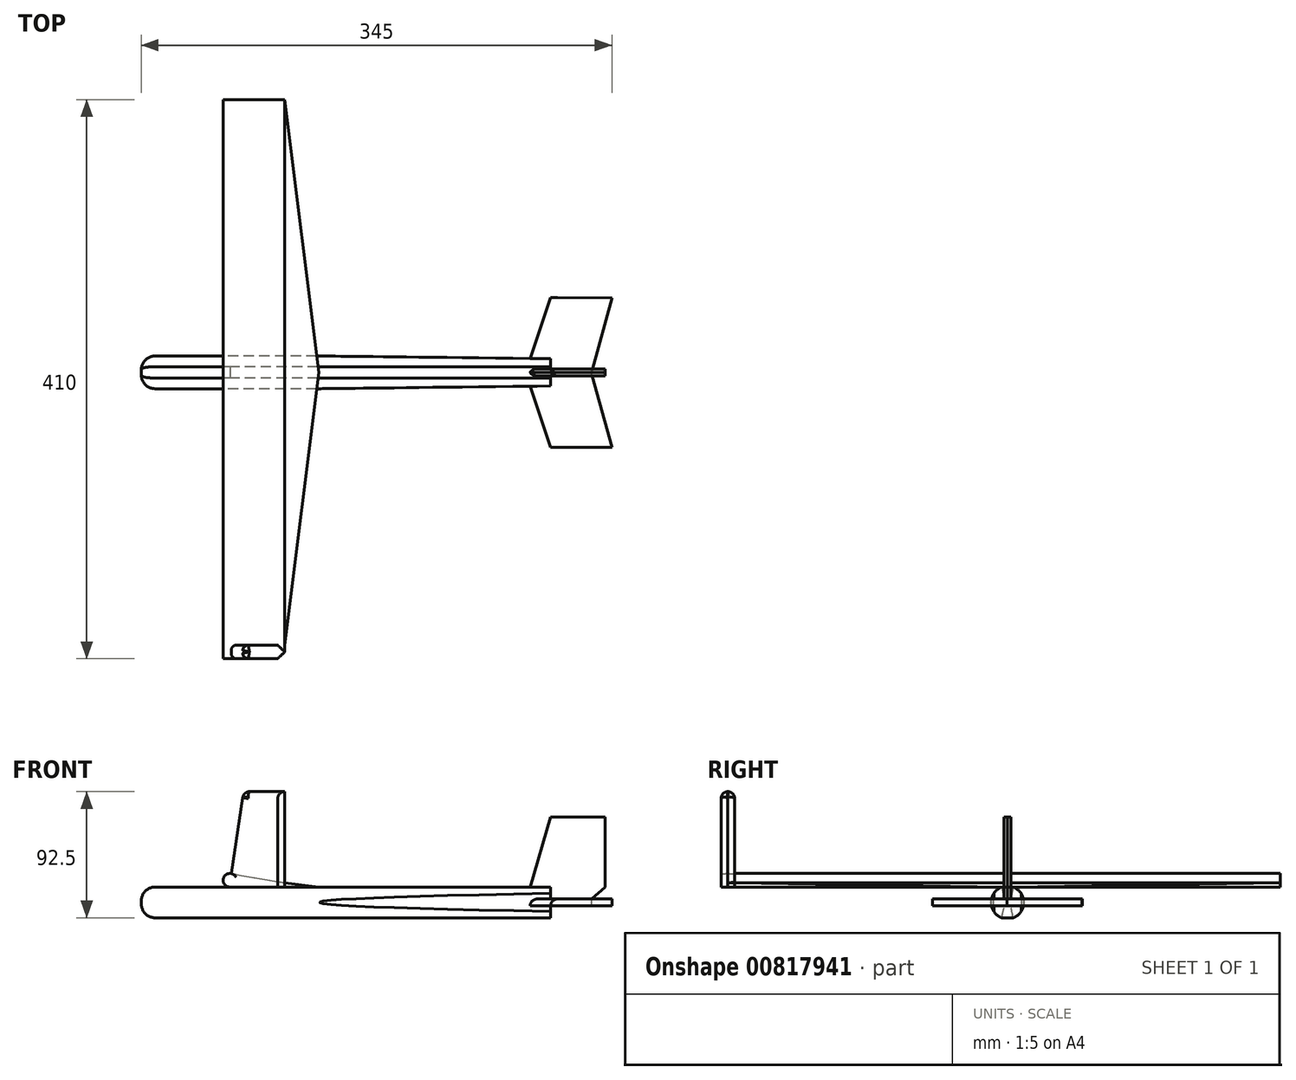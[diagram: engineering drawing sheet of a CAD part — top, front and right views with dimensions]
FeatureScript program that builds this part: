
annotation { "Feature Type Name" : "Feature", "Feature Type Description" : "" }
export const myFeature = defineFeature(function(context is Context, id is Id, definition is map)
    precondition{}
    {
        {
            var Q0;
            Q0=qCreatedBy(makeId("Top.planeOp"),FACE);
            var sketch = newSketch(context, id + "F0", { "sketchPlane" : qUnion([Q0])});
            skLineSegment(sketch, "E0", {"start": v(0, 0) * mm, "end": v(0, 200) * mm});
            skLineSegment(sketch, "E1", {"start": v(0, 0) * mm, "end": v(0, -200) * mm});
            skLineSegment(sketch, "E2", {"start": v(0, -200) * mm, "end": v(45, -200) * mm});
            skLineSegment(sketch, "E3", {"start": v(0, 200) * mm, "end": v(45, 200) * mm});
            skLineSegment(sketch, "E4", {"start": v(0, 0) * mm, "end": v(70, 0) * mm, "construction": true});
            skLineSegment(sketch, "E5", {"start": v(45, 200) * mm, "end": v(70, 0) * mm});
            skLineSegment(sketch, "E6", {"start": v(45, -200) * mm, "end": v(70, 0) * mm});
            skSolve(sketch);
        }
        {
            var Q0;
            Q0=makeQuery(id+"F0.imprint","IMPRINT",FACE,{"disambiguationData":[TD([[makeQuery(id+"F0.imprint","IMPRINT",EDGE,{"derivedFrom":sQuery(id+"F0.wireOp",EDGE,"E0")}),-1.0]])]});
            extrude(context, id + "F1", {"entities" : qUnion([Q0]), "depth" : 10 * mm, "offsetDistance" : 25 * mm});
        }
        {
            var Q0;
            Q0=makeQuery(id+"F1.opExtrude","SWEPT_FACE",FACE,{"disambiguationData":[OSD([sQuery(id+"F0.wireOp",EDGE,"E2")])]});
            var sketch = newSketch(context, id + "F2", { "sketchPlane" : qUnion([Q0])});
            skLineSegment(sketch, "E7.0.0", {"start": v(0, 0) * mm, "end": v(45, 0) * mm});
            skLineSegment(sketch, "E7.0.1", {"start": v(45, 0) * mm, "end": v(45, 10) * mm});
            skLineSegment(sketch, "E7.0.2", {"start": v(45, 10) * mm, "end": v(0, 10) * mm});
            skLineSegment(sketch, "E7.0.3", {"start": v(0, 10) * mm, "end": v(0, 5) * mm});
            skLineSegment(sketch, "E8.0.0", {"start": v(45, 0) * mm, "end": v(70, 0) * mm});
            skLineSegment(sketch, "E8.0.1", {"start": v(70, 0) * mm, "end": v(70, 10) * mm});
            skLineSegment(sketch, "E8.0.2", {"start": v(70, 10) * mm, "end": v(45, 10) * mm});
            skLineSegment(sketch, "E8.0.3", {"start": v(45, 10) * mm, "end": v(45, 0) * mm});
            skArc(sketch, "E9", {"start": v(5.87, 9.92) * mm, "mid": v(0.02, 5.44) * mm, "end": v(5, 0) * mm});
            skPoint(sketch, "E9.centerSnap0", {"position": v(0, 5) * mm});
            skLineSegment(sketch, "E10", {"start": v(5.87, 9.92) * mm, "end": v(45, 3) * mm});
            skLineSegment(sketch, "E11", {"start": v(45, 3) * mm, "end": v(70, 0) * mm});
            skSolve(sketch);
        }
        {
            var Q0;
            {var subQ5=sQuery(id+"F2.wireOp",EDGE,"E10");Q0=makeQuery(id+"F2.imprint","IMPRINT",FACE,{"disambiguationData":[TD([[makeQuery(id+"F2.imprint","IMPRINT",EDGE,{"derivedFrom":subQ5}),1.0]])]});}
            var Q1;
            Q1=makeQuery(id+"F2.imprint","IMPRINT",FACE,{"disambiguationData":[TD([[makeQuery(id+"F2.imprint","IMPRINT",EDGE,{"derivedFrom":sQuery(id+"F2.wireOp",EDGE,"E8.0.1")}),1.0]])]});
            var Q2;
            {var subQ0=sQuery(id+"F2.wireOp",EDGE,"E7.0.3");Q2=makeQuery(id+"F2.imprint","IMPRINT",FACE,{"disambiguationData":[TD([[makeQuery(id+"F2.imprint","IMPRINT",EDGE,{"derivedFrom":subQ0}),1.0]])]});}
            var Q3;
            {var subQ0=sQuery(id+"F2.wireOp",EDGE,"E7.0.0");var subQ3=sQuery(id+"F2.wireOp",EDGE,"E9");var subQ4=makeQuery(id+"F2.imprint","INTERSECT",VERTEX,{"derivedFrom":[subQ0,subQ3]});Q3=makeQuery(id+"F2.imprint","IMPRINT",FACE,{"disambiguationData":[TD([[makeQuery(id+"F2.imprint","IMPRINT",EDGE,{"disambiguationData":[TD([[subQ4,1.0]])],"derivedFrom":subQ0}),1.0]])]});}
            extrude(context, id + "F3", {"entities" : qUnion([Q0, Q1, Q2, Q3]), "operationType" : NewBodyOperationType.REMOVE, "oppositeDirection" : true, "depth" : 400 * mm, "offsetDistance" : 25 * mm});
        }
        {
            var Q0;
            Q0=qCreatedBy(makeId("Top.planeOp"),FACE);
            var sketch = newSketch(context, id + "F4", { "sketchPlane" : qUnion([Q0])});
            skLineSegment(sketch, "E12", {"start": v(0, 12) * mm, "end": v(0, -12) * mm});
            skLineSegment(sketch, "E13", {"start": v(0, -12) * mm, "end": v(-60, -12) * mm});
            skLineSegment(sketch, "E14", {"start": v(-60, -12) * mm, "end": v(-60, 12) * mm});
            skLineSegment(sketch, "E15", {"start": v(-60, 12) * mm, "end": v(0, 12) * mm});
            skLineSegment(sketch, "E16", {"start": v(0, -12) * mm, "end": v(70, -12) * mm});
            skLineSegment(sketch, "E17", {"start": v(70, -12) * mm, "end": v(70, 12) * mm});
            skLineSegment(sketch, "E18", {"start": v(70, 12) * mm, "end": v(0, 12) * mm});
            skLineSegment(sketch, "E19", {"start": v(0, 0) * mm, "end": v(240, 0) * mm, "construction": true});
            skPoint(sketch, "E19.endSnap0", {"position": v(70, 0) * mm});
            skLineSegment(sketch, "E20", {"start": v(240, -10) * mm, "end": v(240, 10) * mm});
            skLineSegment(sketch, "E21", {"start": v(240, -10) * mm, "end": v(70, -12) * mm});
            skLineSegment(sketch, "E22", {"start": v(70, 12) * mm, "end": v(240, 10) * mm});
            skSolve(sketch);
        }
        {
            var Q0;
            Q0=makeQuery(id+"F4.imprint","IMPRINT",FACE,{"disambiguationData":[TD([[makeQuery(id+"F4.imprint","IMPRINT",EDGE,{"derivedFrom":sQuery(id+"F4.wireOp",EDGE,"E12")}),1.0]])]});
            var Q1;
            Q1=makeQuery(id+"F4.imprint","IMPRINT",FACE,{"disambiguationData":[TD([[makeQuery(id+"F4.imprint","IMPRINT",EDGE,{"derivedFrom":sQuery(id+"F4.wireOp",EDGE,"E12")}),-1.0]])]});
            var Q2;
            Q2=makeQuery(id+"F4.imprint","IMPRINT",FACE,{"disambiguationData":[TD([[makeQuery(id+"F4.imprint","IMPRINT",EDGE,{"derivedFrom":sQuery(id+"F4.wireOp",EDGE,"E17")}),-1.0]])]});
            extrude(context, id + "F5", {"entities" : qUnion([Q0, Q1, Q2]), "operationType" : NewBodyOperationType.ADD, "oppositeDirection" : true, "depth" : 22.5 * mm, "offsetDistance" : 25 * mm});
        }
        {
            var Q0;
            Q0=makeQuery(id+"F5.opExtrude","SWEPT_FACE",FACE,{"disambiguationData":[OSD([sQuery(id+"F4.wireOp",EDGE,"E14")])]});
            var sketch = newSketch(context, id + "F6", { "sketchPlane" : qUnion([Q0])});
            skLineSegment(sketch, "E23.0.0", {"start": v(12, 0) * mm, "end": v(-12, 0) * mm});
            skLineSegment(sketch, "E23.0.1", {"start": v(-12, 0) * mm, "end": v(-12, -22.5) * mm});
            skLineSegment(sketch, "E23.0.2", {"start": v(-12, -22.5) * mm, "end": v(12, -22.5) * mm});
            skLineSegment(sketch, "E23.0.3", {"start": v(12, -22.5) * mm, "end": v(12, 0) * mm});
            skCircle(sketch, "E24", {"center": v(0, -11.25) * mm, "radius": 12 * mm});
            skPoint(sketch, "E24.centerSnap0", {"position": v(-12, -11.25) * mm});
            skSolve(sketch);
        }
        {
            var Q0;
            {var subQ0=sQuery(id+"F6.wireOp",EDGE,"E23.0.1");var subQ1=sQuery(id+"F6.wireOp",EDGE,"E23.0.0");var subQ2=makeQuery(id+"F6.imprint","INTERSECT",VERTEX,{"derivedFrom":[subQ1,subQ0]});Q0=makeQuery(id+"F6.imprint","IMPRINT",FACE,{"disambiguationData":[TD([[makeQuery(id+"F6.imprint","IMPRINT",EDGE,{"disambiguationData":[TD([[subQ2,1.0]])],"derivedFrom":subQ1}),1.0]])]});}
            var Q1;
            {var subQ0=sQuery(id+"F6.wireOp",EDGE,"E23.0.3");var subQ1=sQuery(id+"F6.wireOp",EDGE,"E23.0.0");var subQ2=makeQuery(id+"F6.imprint","INTERSECT",VERTEX,{"derivedFrom":[subQ1,subQ0]});Q1=makeQuery(id+"F6.imprint","IMPRINT",FACE,{"disambiguationData":[TD([[makeQuery(id+"F6.imprint","IMPRINT",EDGE,{"disambiguationData":[TD([[subQ2,-1.0]])],"derivedFrom":subQ1}),1.0]])]});}
            var Q2;
            {var subQ0=sQuery(id+"F6.wireOp",EDGE,"E23.0.3");var subQ1=sQuery(id+"F6.wireOp",EDGE,"E23.0.2");var subQ2=makeQuery(id+"F6.imprint","INTERSECT",VERTEX,{"derivedFrom":[subQ1,subQ0]});Q2=makeQuery(id+"F6.imprint","IMPRINT",FACE,{"disambiguationData":[TD([[makeQuery(id+"F6.imprint","IMPRINT",EDGE,{"disambiguationData":[TD([[subQ2,-1.0]])],"derivedFrom":subQ1}),-1.0]])]});}
            var Q3;
            {var subQ0=sQuery(id+"F6.wireOp",EDGE,"E23.0.2");var subQ1=sQuery(id+"F6.wireOp",EDGE,"E23.0.1");var subQ2=makeQuery(id+"F6.imprint","INTERSECT",VERTEX,{"derivedFrom":[subQ1,subQ0]});Q3=makeQuery(id+"F6.imprint","IMPRINT",FACE,{"disambiguationData":[TD([[makeQuery(id+"F6.imprint","IMPRINT",EDGE,{"disambiguationData":[TD([[subQ2,-1.0]])],"derivedFrom":subQ1}),-1.0]])]});}
            extrude(context, id + "F7", {"entities" : qUnion([Q0, Q1, Q2, Q3]), "operationType" : NewBodyOperationType.REMOVE, "oppositeDirection" : true, "depth" : 300 * mm, "offsetDistance" : 25 * mm});
        }
        {
            var Q0;
            Q0=makeQuery(id+"F5.opExtrude","SWEPT_FACE",FACE,{"disambiguationData":[OSD([sQuery(id+"F4.wireOp",EDGE,"E14")])]});
            fillet(context, id + "F8", {"entities" : qUnion([Q0]), "radius" : 10 * mm, "tangentPropagation" : true, "allowEdgeOverflow" : false});
        }
        {
            var Q0;
            {var subQ0=sQuery(id+"F0.wireOp",EDGE,"E5");var subQ2=sQuery(id+"F4.wireOp",EDGE,"E21");var subQ3=sQuery(id+"F4.wireOp",EDGE,"E16");var subQ4=sQuery(id+"F4.wireOp",EDGE,"E13");var subQ5=sQuery(id+"F4.wireOp",EDGE,"E18");var subQ6=sQuery(id+"F4.wireOp",EDGE,"E15");var subQ7=sQuery(id+"F4.wireOp",EDGE,"E20");var subQ8=sQuery(id+"F4.wireOp",EDGE,"E22");Q0=makeQuery(id+"F5.boolean.opBoolean","SPLIT",FACE,{"disambiguationData":[TD([makeQuery(id+"F1.opExtrude","SWEPT_FACE",FACE,{"disambiguationData":[OSD([subQ0])]})])],"derivedFrom":makeQuery(id+"F5.opExtrude","CAP_FACE",FACE,{"disambiguationData":[OSD([subQ4,sQuery(id+"F4.wireOp",EDGE,"E14"),subQ6,subQ3,subQ5,subQ7,subQ2,subQ8])],"isStart":true})});}
            cPlane(context, id + "F9", {"entities" : qUnion([Q0]), "cplaneType" : CPlaneType.OFFSET, "offset" : 11.25 * mm, "oppositeDirection" : true, "width" : 150 * mm, "height" : 150 * mm});
        }
        {
            var Q0;
            Q0=qCreatedBy(id+"F9.planeOp",FACE);
            var sketch = newSketch(context, id + "F10", { "sketchPlane" : qUnion([Q0])});
            skLineSegment(sketch, "E25.0", {"start": v(240, 10) * mm, "end": v(70, 12) * mm});
            skLineSegment(sketch, "E26.0", {"start": v(240, -4.18) * mm, "end": v(240, 4.18) * mm});
            skLineSegment(sketch, "E27.0", {"start": v(240, 4.18) * mm, "end": v(240, 10) * mm});
            skLineSegment(sketch, "E28.0", {"start": v(240, -10) * mm, "end": v(240, -4.18) * mm});
            skLineSegment(sketch, "E29.0", {"start": v(240, -10) * mm, "end": v(70, -12) * mm});
            skLineSegment(sketch, "E30", {"start": v(240, 0) * mm, "end": v(225, 0.18) * mm, "construction": true});
            skLineSegment(sketch, "E31", {"start": v(240, 0) * mm, "end": v(270, -0.35) * mm, "construction": true});
            skPoint(sketch, "E32", {"position": v(230, 0.12) * mm});
            skLineSegment(sketch, "E33", {"start": v(230, 0.12) * mm, "end": v(230, 10.12) * mm, "construction": true});
            skLineSegment(sketch, "E34", {"start": v(230, 0.12) * mm, "end": v(230, -10.12) * mm, "construction": true});
            skLineSegment(sketch, "E35", {"start": v(225, -10.18) * mm, "end": v(225, 10.18) * mm, "construction": true});
            skLineSegment(sketch, "E36", {"start": v(240, 0) * mm, "end": v(240, 55) * mm, "construction": true});
            skLineSegment(sketch, "E37", {"start": v(240, 0) * mm, "end": v(240, -55) * mm, "construction": true});
            skLineSegment(sketch, "E38", {"start": v(240, -55) * mm, "end": v(285, -55) * mm});
            skLineSegment(sketch, "E39", {"start": v(285, -55) * mm, "end": v(270, -0.35) * mm});
            skLineSegment(sketch, "E40", {"start": v(240, 55) * mm, "end": v(285, 54.47) * mm});
            skLineSegment(sketch, "E41", {"start": v(285, 54.47) * mm, "end": v(270, -0.35) * mm});
            skLineSegment(sketch, "E42", {"start": v(240, 55) * mm, "end": v(225, 10.18) * mm});
            skLineSegment(sketch, "E43", {"start": v(240, -55) * mm, "end": v(225, -10.18) * mm});
            skSolve(sketch);
        }
        {
            var Q0;
            Q0=makeQuery(id+"F10.imprint","IMPRINT",FACE,{"disambiguationData":[TD([[makeQuery(id+"F10.imprint","IMPRINT",EDGE,{"derivedFrom":sQuery(id+"F10.wireOp",EDGE,"E26.0")}),-1.0]])]});
            extrude(context, id + "F11", {"entities" : qUnion([Q0]), "operationType" : NewBodyOperationType.ADD, "endBound" : BoundingType.SYMMETRIC, "depth" : 5 * mm, "offsetDistance" : 25 * mm});
        }
        {
            var Q0;
            Q0=qCreatedBy(makeId("Front.planeOp"),FACE);
            var sketch = newSketch(context, id + "F12", { "sketchPlane" : qUnion([Q0])});
            skLineSegment(sketch, "E44.0", {"start": v(240, -8.75) * mm, "end": v(285, -8.75) * mm});
            skLineSegment(sketch, "E45.0", {"start": v(240, -8.75) * mm, "end": v(240, -4.62) * mm});
            skLineSegment(sketch, "E46.0", {"start": v(240, -4.62) * mm, "end": v(240, 0) * mm});
            skLineSegment(sketch, "E47.0", {"start": v(240, 0) * mm, "end": v(69.48, 0) * mm});
            skLineSegment(sketch, "E48.0", {"start": v(240, -8.75) * mm, "end": v(225, -8.75) * mm});
            skLineSegment(sketch, "E49", {"start": v(225, -8.75) * mm, "end": v(225, 0) * mm, "construction": true});
            skLineSegment(sketch, "E50", {"start": v(240, -8.75) * mm, "end": v(240, 51.25) * mm, "construction": true});
            skPoint(sketch, "E51", {"position": v(270, -8.75) * mm});
            skLineSegment(sketch, "E52", {"start": v(225, 0) * mm, "end": v(240, 51.25) * mm});
            skLineSegment(sketch, "E53", {"start": v(280, 51.25) * mm, "end": v(240, 51.25) * mm});
            skLineSegment(sketch, "E54", {"start": v(280, 0) * mm, "end": v(270, -8.75) * mm});
            skLineSegment(sketch, "E55", {"start": v(280, 51.25) * mm, "end": v(280, 0) * mm});
            skSolve(sketch);
        }
        {
            var Q0;
            {var subQ3=sQuery(id+"F12.wireOp",EDGE,"E45.0");Q0=makeQuery(id+"F12.imprint","IMPRINT",FACE,{"disambiguationData":[TD([[makeQuery(id+"F12.imprint","IMPRINT",EDGE,{"derivedFrom":subQ3}),-1.0]])]});}
            extrude(context, id + "F13", {"entities" : qUnion([Q0]), "operationType" : NewBodyOperationType.ADD, "endBound" : BoundingType.SYMMETRIC, "depth" : 5 * mm, "offsetDistance" : 25 * mm, "hasDraft" : true, "draftAngle" : 3 * degree});
        }
        {
            var Q0;
            Q0=makeQuery(id+"F11.opExtrude","CAP_EDGE",EDGE,{"disambiguationData":[OSD([sQuery(id+"F10.wireOp",EDGE,"E42")])],"isStart":false});
            var Q1;
            Q1=makeQuery(id+"F11.opExtrude","CAP_EDGE",EDGE,{"disambiguationData":[OSD([sQuery(id+"F10.wireOp",EDGE,"E43")])],"isStart":false});
            fillet(context, id + "F14", {"entities" : qUnion([Q0, Q1]), "radius" : 5 * mm, "tangentPropagation" : true, "allowEdgeOverflow" : false});
        }
        {
            var Q0;
            Q0=makeQuery(id+"F13.opExtrude","CAP_EDGE",EDGE,{"disambiguationData":[OSD([sQuery(id+"F12.wireOp",EDGE,"E52")])],"isStart":true});
            var Q1;
            Q1=makeQuery(id+"F13.opExtrude","CAP_EDGE",EDGE,{"disambiguationData":[OSD([sQuery(id+"F12.wireOp",EDGE,"E52")])],"isStart":false});
            fillet(context, id + "F15", {"entities" : qUnion([Q0, Q1]), "radius" : 5 * mm, "tangentPropagation" : true, "allowEdgeOverflow" : false});
        }
        {
            var Q0;
            Q0=makeQuery(id+"F1.opExtrude","SWEPT_FACE",FACE,{"disambiguationData":[OSD([sQuery(id+"F0.wireOp",EDGE,"E2")])]});
            var sketch = newSketch(context, id + "F16", { "sketchPlane" : qUnion([Q0])});
            skArc(sketch, "E56", {"start": v(5.87, 9.92) * mm, "mid": v(0.02, 5.44) * mm, "end": v(5, 0) * mm});
            skLineSegment(sketch, "E57", {"start": v(5, 0) * mm, "end": v(5.87, 9.92) * mm});
            skSolve(sketch);
        }
        {
            var Q0;
            Q0 = qSketchRegion(id + "F16", true);
            extrude(context, id + "F17", {"entities" : qUnion([Q0]), "operationType" : NewBodyOperationType.ADD, "depth" : 10 * mm, "offsetDistance" : 25 * mm});
        }
        {
            var Q0;
            Q0=makeQuery(id+"F1.opExtrude","SWEPT_FACE",FACE,{"disambiguationData":[OSD([sQuery(id+"F0.wireOp",EDGE,"E2")])]});
            var sketch = newSketch(context, id + "F18", { "sketchPlane" : qUnion([Q0])});
            skLineSegment(sketch, "E58", {"start": v(45, 0) * mm, "end": v(45, 70) * mm});
            skLineSegment(sketch, "E59", {"start": v(45, 70) * mm, "end": v(15, 70) * mm});
            skLineSegment(sketch, "E60", {"start": v(15, 70) * mm, "end": v(5.87, 9.92) * mm});
            skLineSegment(sketch, "E61", {"start": v(5.87, 9.92) * mm, "end": v(5, 0) * mm});
            skLineSegment(sketch, "E62", {"start": v(5, 0) * mm, "end": v(45, 0) * mm});
            skSolve(sketch);
        }
        {
            var Q0;
            Q0 = qSketchRegion(id + "F18", true);
            extrude(context, id + "F19", {"entities" : qUnion([Q0]), "operationType" : NewBodyOperationType.ADD, "depth" : 10 * mm, "offsetDistance" : 25 * mm});
        }
        {
            var Q0;
            Q0=makeQuery(id+"F19.opExtrude","CAP_EDGE",EDGE,{"disambiguationData":[OSD([sQuery(id+"F18.wireOp",EDGE,"E60")])],"isStart":true});
            var Q1;
            Q1=makeQuery(id+"F19.opExtrude","CAP_EDGE",EDGE,{"disambiguationData":[OSD([sQuery(id+"F18.wireOp",EDGE,"E60")])],"isStart":false});
            fillet(context, id + "F20", {"entities" : qUnion([Q0, Q1]), "radius" : 4 * mm, "tangentPropagation" : true, "allowEdgeOverflow" : false});
        }
        {
            var Q0;
            Q0=makeQuery(id+"F19.opExtrude","CAP_EDGE",EDGE,{"disambiguationData":[OSD([sQuery(id+"F18.wireOp",EDGE,"E58")])],"isStart":false});
            var Q1;
            Q1=makeQuery(id+"F19.boolean.opBoolean","SPLIT",EDGE,{"derivedFrom":makeQuery(id+"F19.opExtrude","CAP_EDGE",EDGE,{"disambiguationData":[OSD([sQuery(id+"F18.wireOp",EDGE,"E58")])],"isStart":true})});
            chamfer(context, id + "F21", {"entities" : qUnion([Q0, Q1]), "width" : 5 * mm, "tangentPropagation" : true});
        }
        {
            var Q0;
            Q0=makeQuery(id+"F19.opExtrude","CAP_EDGE",EDGE,{"disambiguationData":[OSD([sQuery(id+"F18.wireOp",EDGE,"E59")])],"isStart":false});
            fillet(context, id + "F22", {"entities" : qUnion([Q0]), "radius" : 5 * mm, "tangentPropagation" : true, "allowEdgeOverflow" : false});
        }
    });
